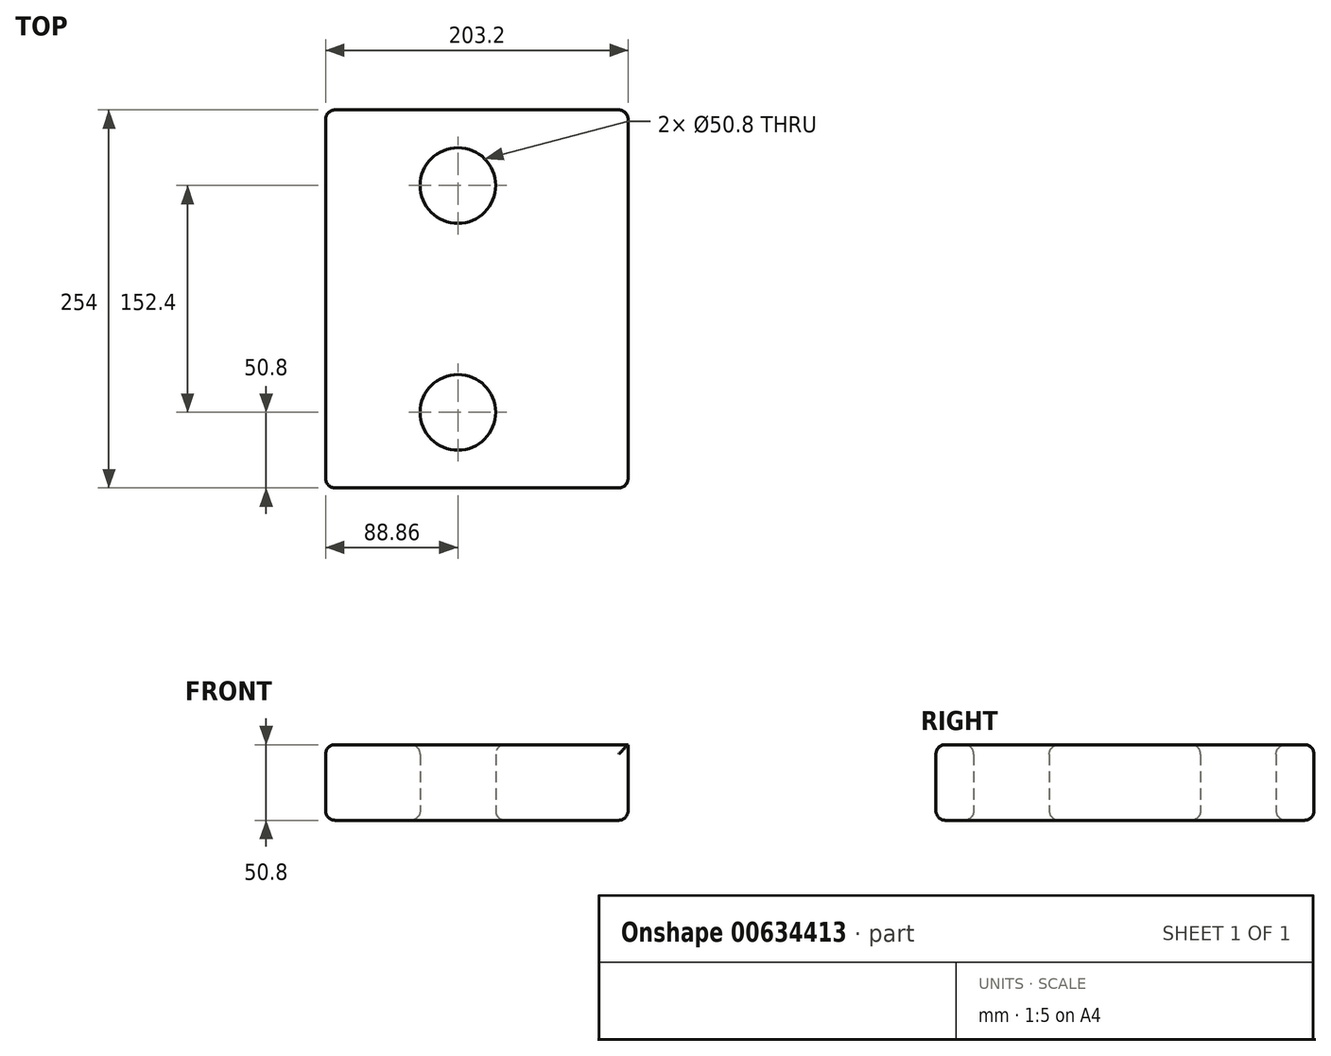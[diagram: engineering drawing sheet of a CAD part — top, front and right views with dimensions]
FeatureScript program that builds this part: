
annotation { "Feature Type Name" : "Feature", "Feature Type Description" : "" }
export const myFeature = defineFeature(function(context is Context, id is Id, definition is map)
    precondition{}
    {
        {
            var Q0;
            Q0=qCreatedBy(makeId("Top.planeOp"),FACE);
            var sketch = newSketch(context, id + "F0", { "sketchPlane" : qUnion([Q0])});
            skLineSegment(sketch, "E0.bottom", {"start": v(0, 0) * mm, "end": v(203.2, 0) * mm});
            skLineSegment(sketch, "E0.top", {"start": v(0, 254) * mm, "end": v(203.2, 254) * mm});
            skLineSegment(sketch, "E0.left", {"start": v(0, 0) * mm, "end": v(0, 254) * mm});
            skLineSegment(sketch, "E0.right", {"start": v(203.2, 0) * mm, "end": v(203.2, 254) * mm});
            skCircle(sketch, "E1", {"center": v(88.86, 203.2) * mm, "radius": 25.4 * mm});
            skLineSegment(sketch, "E2", {"start": v(0, 127) * mm, "end": v(203.2, 127) * mm, "construction": true});
            skCircle(sketch, "E3.MirrorC", {"center": v(88.86, 50.8) * mm, "radius": 25.4 * mm});
            skSolve(sketch);
        }
        {
            var Q0;
            Q0=makeQuery(id+"F0.imprint","IMPRINT",FACE,{"disambiguationData":[TD([[makeQuery(id+"F0.imprint","IMPRINT",EDGE,{"derivedFrom":sQuery(id+"F0.wireOp",EDGE,"E0.bottom")}),1.0]])]});
            extrude(context, id + "F1", {"entities" : qUnion([Q0]), "depth" : 50.8 * mm, "offsetDistance" : 25.4 * mm});
        }
        {
            var Q0;
            Q0=makeQuery(id+"F1.opExtrude","CAP_EDGE",EDGE,{"disambiguationData":[OSD([sQuery(id+"F0.wireOp",EDGE,"E0.left")])],"isStart":true});
            var Q1;
            Q1=makeQuery(id+"F1.opExtrude","CAP_EDGE",EDGE,{"disambiguationData":[OSD([sQuery(id+"F0.wireOp",EDGE,"E0.left")])],"isStart":false});
            var Q2;
            Q2=makeQuery(id+"F1.opExtrude","CAP_EDGE",EDGE,{"disambiguationData":[OSD([sQuery(id+"F0.wireOp",EDGE,"E0.top")])],"isStart":false});
            var Q3;
            Q3=makeQuery(id+"F1.opExtrude","CAP_EDGE",EDGE,{"disambiguationData":[OSD([sQuery(id+"F0.wireOp",EDGE,"E1")])],"isStart":false});
            var Q4;
            Q4=makeQuery(id+"F1.opExtrude","CAP_EDGE",EDGE,{"disambiguationData":[OSD([sQuery(id+"F0.wireOp",EDGE,"E3.MirrorC")])],"isStart":false});
            var Q5;
            Q5=makeQuery(id+"F1.opExtrude","CAP_EDGE",EDGE,{"disambiguationData":[OSD([sQuery(id+"F0.wireOp",EDGE,"E0.top")])],"isStart":true});
            var Q6;
            Q6=makeQuery(id+"F1.opExtrude","SWEPT_EDGE",EDGE,{"disambiguationData":[OSD([sQuery(id+"F0.wireOp",EDGE,"E0.top"),sQuery(id+"F0.wireOp",EDGE,"E0.left")])]});
            var Q7;
            Q7=makeQuery(id+"F1.opExtrude","SWEPT_EDGE",EDGE,{"disambiguationData":[OSD([sQuery(id+"F0.wireOp",EDGE,"E0.top"),sQuery(id+"F0.wireOp",EDGE,"E0.right")])]});
            var Q8;
            Q8=makeQuery(id+"F1.opExtrude","CAP_EDGE",EDGE,{"disambiguationData":[OSD([sQuery(id+"F0.wireOp",EDGE,"E1")])],"isStart":true});
            var Q9;
            Q9=makeQuery(id+"F1.opExtrude","CAP_EDGE",EDGE,{"disambiguationData":[OSD([sQuery(id+"F0.wireOp",EDGE,"E3.MirrorC")])],"isStart":true});
            var Q10;
            Q10=makeQuery(id+"F1.opExtrude","CAP_FACE",FACE,{"disambiguationData":[OSD([sQuery(id+"F0.wireOp",EDGE,"E0.bottom"),sQuery(id+"F0.wireOp",EDGE,"E0.top"),sQuery(id+"F0.wireOp",EDGE,"E0.left"),sQuery(id+"F0.wireOp",EDGE,"E0.right"),sQuery(id+"F0.wireOp",EDGE,"E1"),sQuery(id+"F0.wireOp",EDGE,"E3.MirrorC")])],"isStart":true});
            fillet(context, id + "F2", {"entities" : qUnion([Q0, Q1, Q2, Q3, Q4, Q5, Q6, Q7, Q8, Q9, Q10]), "radius" : 6.35 * mm, "tangentPropagation" : true, "allowEdgeOverflow" : false});
        }
        {
            var Q0;
            {var subQ0=sQuery(id+"F0.wireOp",EDGE,"E0.bottom");Q0=makeQuery(id+"F2.opFillet","BLEND_EDGE",EDGE,{"blendedFrom":[makeQuery(id+"F1.opExtrude","CAP_EDGE",EDGE,{"disambiguationData":[OSD([subQ0])],"isStart":true}),makeQuery(id+"F1.opExtrude","SWEPT_FACE",FACE,{"disambiguationData":[OSD([subQ0])]})],"blendedInto":[makeQuery(id+"F1.opExtrude","SWEPT_FACE",FACE,{"disambiguationData":[OSD([subQ0])]})]});}
            var Q1;
            Q1=makeQuery(id+"F2.opFillet","BLEND_FACE",FACE,{"disambiguationData":[OSD([sQuery(id+"F0.wireOp",EDGE,"E0.bottom")])]});
            fillet(context, id + "F3", {"entities" : qUnion([Q0, Q1]), "radius" : 6.35 * mm, "tangentPropagation" : true, "allowEdgeOverflow" : false});
        }
    });
